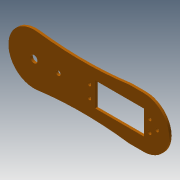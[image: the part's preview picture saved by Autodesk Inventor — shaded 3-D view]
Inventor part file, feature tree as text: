
AUTODESK INVENTOR PART (.ipt)
format: ipt  version: 2013 (Build 170138000, 138)  size: 131,072 bytes
history: native  units: mm
features: sketch x4, extrude x3
ambient origin geometry x8: Origin, YZ Plane, XZ Plane, XY Plane, X Axis, Y Axis, Z Axis, Center Point
bodies: Solid1 (feature_tree)
feature tree (7):
  extrude  "Extrusion1"  Depth=40.2mm
  extrude  "Extrusion2"  Depth=20.0mm
  extrude  "Extrusion3"  Depth=6.0mm
  sketch  "Sketch4"  dims[d25=40.0mm d26=10.0mm d27=3.0mm d28=40.0mm d29=4.0mm d30=2.0mm d31=0.0mm d32=2.0mm d33=0.0mm d34=20.0mm d35=4.0mm d36=2.0mm d37=0.0mm]
  sketch  "Sketch1"  dims[d2=42.0mm d11=40.2mm]
  sketch  "Sketch2"  dims[d13=55.0mm d14=20.0mm]
  sketch  "Sketch3"  dims[d23=3.0mm d24=6.0mm]
